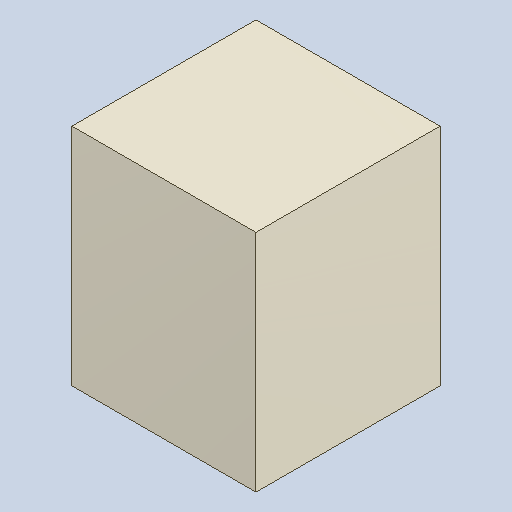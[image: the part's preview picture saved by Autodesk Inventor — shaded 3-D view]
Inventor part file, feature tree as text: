
AUTODESK INVENTOR PART (.ipt)
format: ipt  version: 2023.4 (Build 274418000, 418)  size: 82,944 bytes
history: native  units: mm
features: extrude x1
ambient origin geometry x8: Origin, YZ Plane, XZ Plane, XY Plane, X Axis, Y Axis, Z Axis, Center Point
bodies: Solid1 (feature_tree)
feature tree (1):
  extrude  "Extruded_18"  [1 undecoded]
note: 1 required parameter value undecoded (feature->parameter linkage not recoverable at this tier; creation-order binding heuristic only, values carry confidence <= 0.55)
